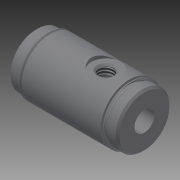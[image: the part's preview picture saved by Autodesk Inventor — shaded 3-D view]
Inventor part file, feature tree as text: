
AUTODESK INVENTOR PART (.ipt)
format: ipt  version: 2014 (Build 180170000, 170)  size: 205,824 bytes
history: native  units: in
note: dims shown in document units (in); Inventor stores cm internally (conversion verified against a paired STEP export)
features: other x49, sketch x5, revolve x4, hole x1, thread x1
ambient origin geometry x8: Origin, YZ Plane, XZ Plane, XY Plane, X Axis, Y Axis, Z Axis, Center Point
bodies: Solid1 (feature_tree)
feature tree (60):
  revolve  "Revolution1"  Angle=360.0deg
  hole  "Hole1"  [1 undecoded]
  revolve  "Revolution2"  [1 undecoded]
  thread  "Thread1"  [1 undecoded]
  revolve  "Revolution3"  [1 undecoded]
  revolve  "Revolution4"  [1 undecoded]
  other  "ba2_XY"
  other  "ba2_YZ"
  other  "ba2_ZX"
  other  "ba2_X"
  other  "ba2_Y"
  other  "ba2_Z"
  other  "ba2_Center"
  other  "centar_XY"
  other  "centar_YZ"
  other  "centar_ZX"
  other  "centar_X"
  other  "centar_Y"
  other  "centar_Z"
  other  "centar_Center"
  other  "d1_XY"
  other  "d1_YZ"
  other  "d1_ZX"
  other  "d1_X"
  other  "d1_Y"
  other  "d1_Z"
  other  "d1_Center"
  other  "d2_XY"
  other  "d2_YZ"
  other  "d2_ZX"
  other  "d2_X"
  other  "d2_Y"
  other  "d2_Z"
  other  "d2_Center"
  other  "to_cyl_A_XY"
  other  "to_cyl_A_YZ"
  other  "to_cyl_A_ZX"
  other  "to_cyl_A_X"
  other  "to_cyl_A_Y"
  other  "to_cyl_A_Z"
  other  "to_cyl_A_Center"
  other  "to_cyl_B_XY"
  other  "to_cyl_B_YZ"
  other  "to_cyl_B_ZX"
  other  "to_cyl_B_X"
  other  "to_cyl_B_Y"
  other  "to_cyl_B_Z"
  other  "to_cyl_B_Center"
  other  "to_rod_A_XY"
  other  "to_rod_A_YZ"
  other  "to_rod_A_ZX"
  other  "to_rod_A_X"
  other  "to_rod_A_Y"
  other  "to_rod_A_Z"
  other  "to_rod_A_Center"
  sketch  "Sketch_1"  dims[d0=360.0deg]
  sketch  "Sketch2"  dims[d1=0.21in d2=0.75in d3=0.375in d4=0.25in d5=0.5635in d6=1.156in d7=0.0in d8=360.0deg]
  sketch  "Sketch_6"  dims[d9=0.0955in d10=0.1018in d11=360.0deg]
  sketch  "Sketch_8"  dims[d12=360.0deg]
  sketch  "Sketch_14"
note: 5 required parameter values undecoded (feature->parameter linkage not recoverable at this tier; creation-order binding heuristic only, values carry confidence <= 0.55)
